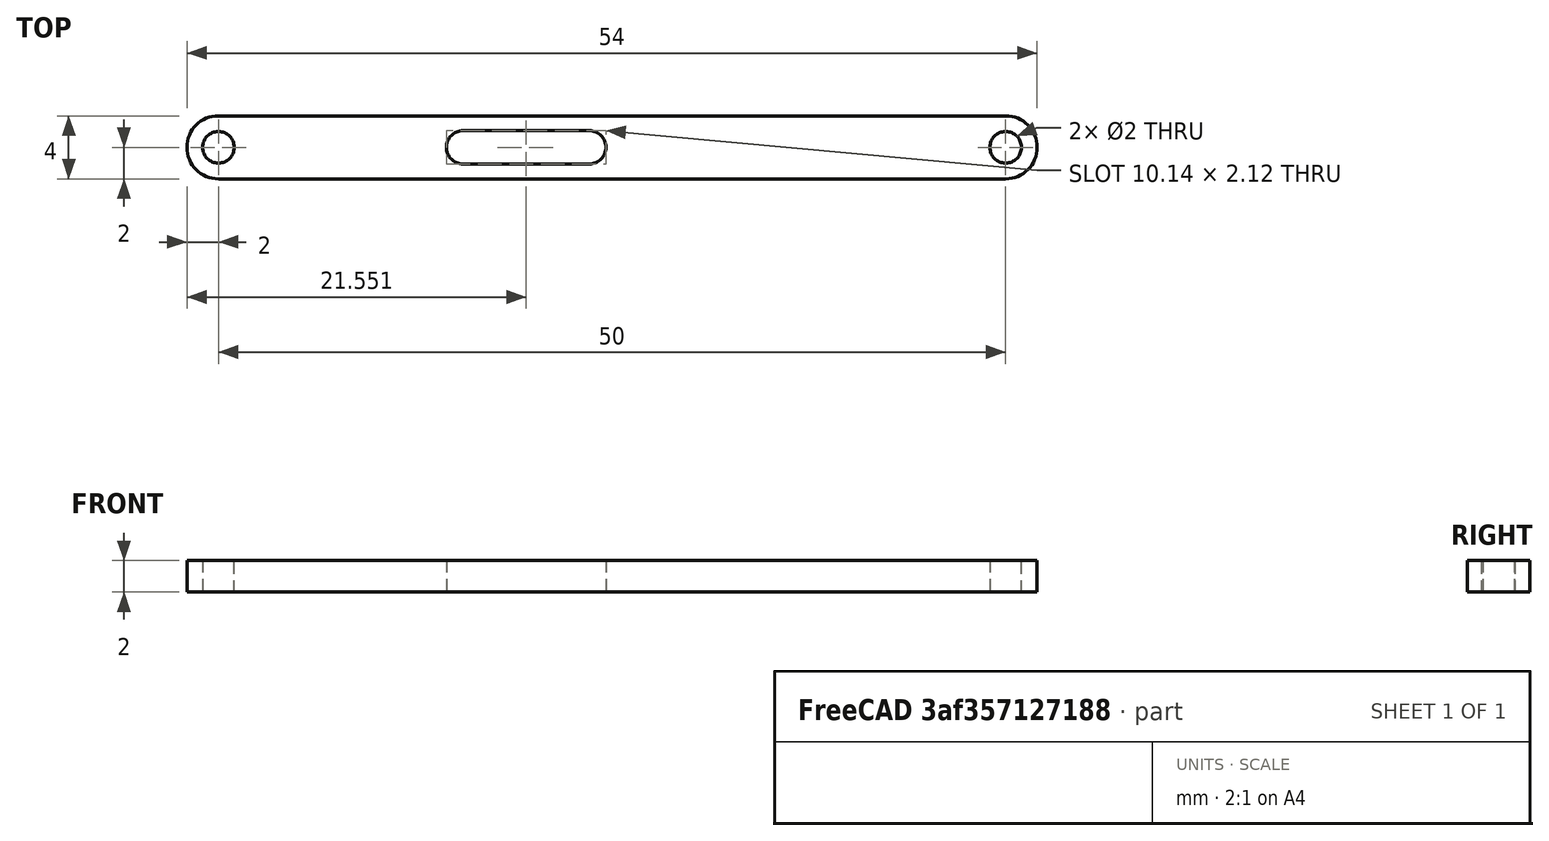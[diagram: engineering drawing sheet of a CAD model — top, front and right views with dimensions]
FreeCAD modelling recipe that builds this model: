
FCSTD DOCUMENT  (FreeCAD 1.0R39109 (Git))
Label: AnimationAndKinematics
License: All rights reserved
LicenseURL: https://en.wikipedia.org/wiki/All_rights_reserved
objects: Sketcher::SketchObject×1, PartDesign::Pad×1, PartDesign::Body×1
note: 6 computed .brp shape members not serialized (recipe doc carries the construction recipe); baked Part::Feature solids carry a one-line shape summary decoded from their .brp

FEATURE [Sketcher::SketchObject] Sketch
  ArcFitTolerance = 1e-06
  AttachmentSupport = -> [XY_Plane]
  FullyConstrained = false
  MakeInternals = false
  MapMode = 5
  sketch-geometry (10):
    g0: ArcOfCircle CenterX=-50 CenterY=0 CenterZ=0 NormalX=0 NormalY=0 NormalZ=1 AngleXU=0 Radius=2 StartAngle=1.5708 EndAngle=4.71239
    g1: ArcOfCircle CenterX=0 CenterY=0 CenterZ=0 NormalX=0 NormalY=0 NormalZ=1 AngleXU=0 Radius=2 StartAngle=4.71239 EndAngle=7.85398
    g2: LineSegment StartX=-50 StartY=2 StartZ=0 EndX=0 EndY=2 EndZ=0
    g3: LineSegment StartX=-50 StartY=-2 StartZ=0 EndX=0 EndY=-2 EndZ=0
    g4: Circle CenterX=0 CenterY=0 CenterZ=0 NormalX=0 NormalY=0 NormalZ=1 AngleXU=0 Radius=1
    g5: Circle CenterX=-50 CenterY=0 CenterZ=0 NormalX=0 NormalY=0 NormalZ=1 AngleXU=0 Radius=1
    g6: ArcOfCircle CenterX=-34.4554 CenterY=0 CenterZ=0 NormalX=0 NormalY=0 NormalZ=1 AngleXU=0 Radius=1.06136 StartAngle=1.5708 EndAngle=4.71239
    g7: ArcOfCircle CenterX=-26.4427 CenterY=0 CenterZ=0 NormalX=0 NormalY=0 NormalZ=1 AngleXU=0 Radius=1.06136 StartAngle=4.71239 EndAngle=7.85398
    g8: LineSegment StartX=-34.4554 StartY=1.06136 StartZ=0 EndX=-26.4427 EndY=1.06136 EndZ=0
    g9: LineSegment StartX=-34.4554 StartY=-1.06136 StartZ=0 EndX=-26.4427 EndY=-1.06136 EndZ=0
  constraints (20):
    c: Tangent(g0,g2) = 1.5708
    c: Tangent(g0,g3) = -1.5708
    c: Tangent(g1,g2) = 1.5708
    c: Tangent(g1,g3) = -1.5708
    c: Equal(g0,g1)
    c: Horizontal(g2)
    c: Coincident(g1,g-1)
    c: DistanceY(g1,g1) = 4
    c: Distance(g1,g0) = 50
    c: Coincident(g4,g1)
    c: Diameter(g4) = 2
    c: Coincident(g5,g0)
    c: Equal(g4,g5)
    c: Tangent(g6,g8) = 1.5708
    c: Tangent(g6,g9) = -1.5708
    c: Tangent(g7,g8) = 1.5708
    c: Tangent(g7,g9) = -1.5708
    c: Equal(g6,g7)
    c: Horizontal(g9)
    c: PointOnObject(g6,g-1)
FEATURE [PartDesign::Pad] Pad
  Direction = (0,0,1)
  Length = 2
  Length2 = 10
  Profile = -> Sketch
  ReferenceAxis = -> Sketch [N_Axis]
  Refine = true
  Suppressed = false
  Type = 0
FEATURE [PartDesign::Body] Body
  AllowCompound = false
  Group = -> [Sketch,Pad]
  Origin = -> Origin
  Tip = -> Pad
